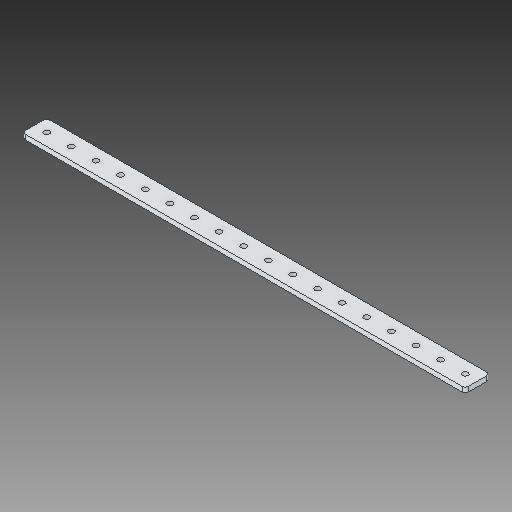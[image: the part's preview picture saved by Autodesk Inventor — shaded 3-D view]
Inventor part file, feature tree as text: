
AUTODESK INVENTOR PART (.ipt)
format: ipt  version: 2018 (Build 220112000, 112)  size: 126,464 bytes
history: native  units: in
note: dims shown in document units (in); Inventor stores cm internally (conversion verified against a paired STEP export)
features: fillet x1
ambient origin geometry x8: Origin, YZ Plane, XZ Plane, XY Plane, X Axis, Y Axis, Z Axis, Center Point
bodies: Solid1 (feature_tree)
feature tree (1):
  fillet  "Fillet1"  [1 undecoded]
note: 1 required parameter value undecoded (feature->parameter linkage not recoverable at this tier; creation-order binding heuristic only, values carry confidence <= 0.55)
